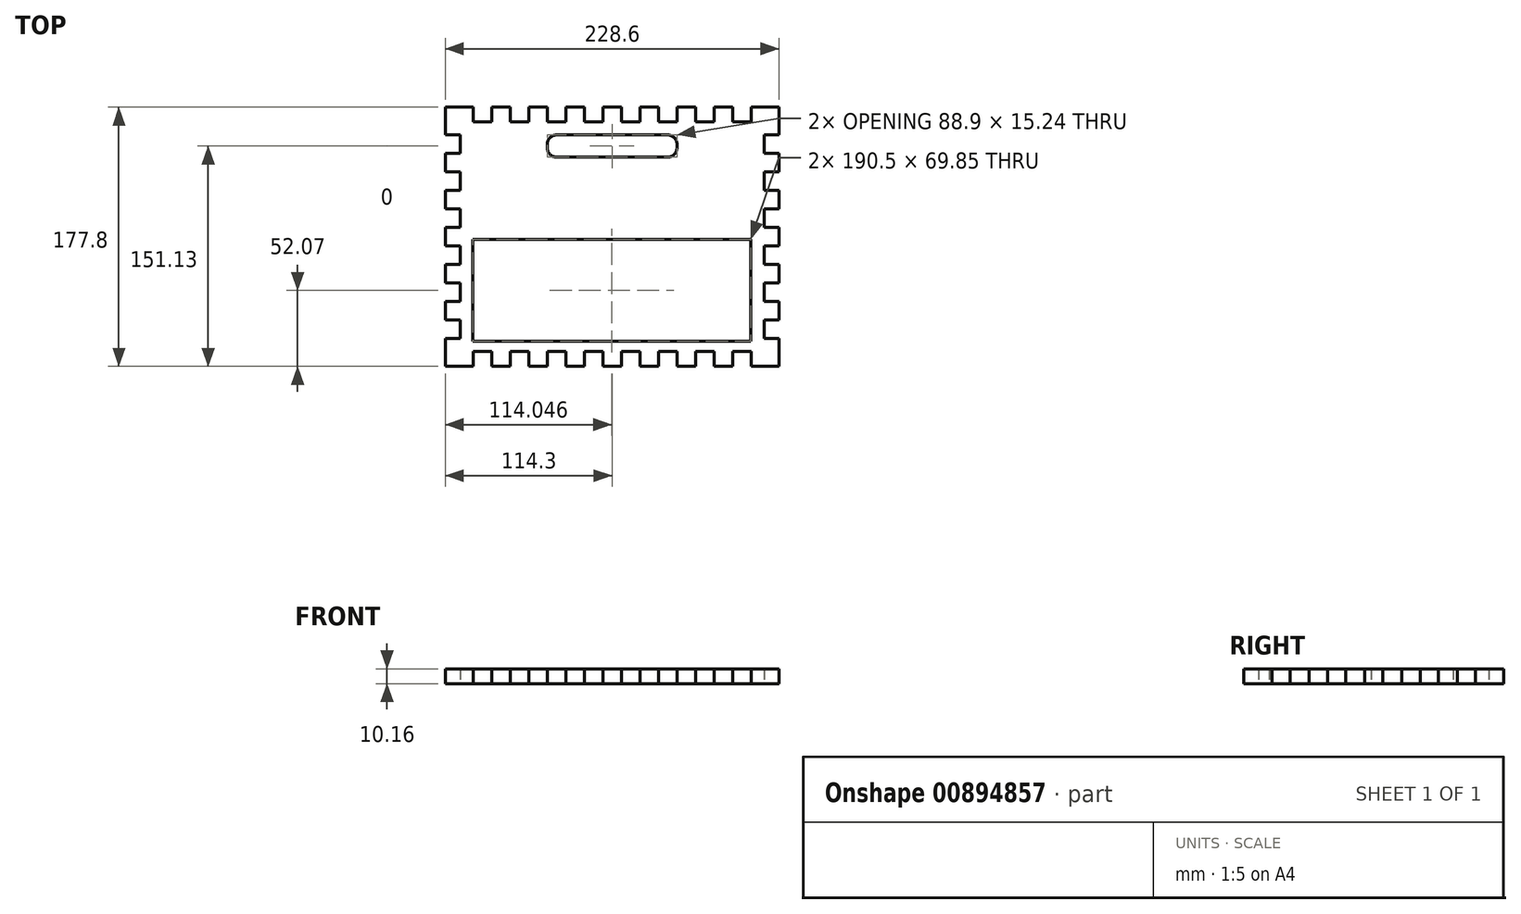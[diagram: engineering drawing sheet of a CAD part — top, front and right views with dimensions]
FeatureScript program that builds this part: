
annotation { "Feature Type Name" : "Feature", "Feature Type Description" : "" }
export const myFeature = defineFeature(function(context is Context, id is Id, definition is map)
    precondition{}
    {
        {
            var Q0;
            Q0=qCreatedBy(makeId("Top.planeOp"),FACE);
            var sketch = newSketch(context, id + "F0", { "sketchPlane" : qUnion([Q0])});
            skLineSegment(sketch, "E0.bottom", {"start": v(0, 0) * mm, "end": v(19.05, 0) * mm});
            skLineSegment(sketch, "E0.left", {"start": v(0, 0) * mm, "end": v(0, -19.05) * mm});
            skLineSegment(sketch, "E1", {"start": v(19.05, 0) * mm, "end": v(19.05, -10.16) * mm});
            skLineSegment(sketch, "E2", {"start": v(19.05, -10.16) * mm, "end": v(31.75, -10.16) * mm});
            skLineSegment(sketch, "E3", {"start": v(31.75, -10.16) * mm, "end": v(31.75, 0) * mm});
            skLineSegment(sketch, "E4", {"start": v(31.75, 0) * mm, "end": v(44.45, 0) * mm});
            skLineSegment(sketch, "E5", {"start": v(44.45, 0) * mm, "end": v(44.45, -10.16) * mm});
            skLineSegment(sketch, "E6", {"start": v(44.45, -10.16) * mm, "end": v(57.15, -10.16) * mm});
            skLineSegment(sketch, "E7", {"start": v(57.15, -10.16) * mm, "end": v(57.15, 0) * mm});
            skLineSegment(sketch, "E8", {"start": v(57.15, 0) * mm, "end": v(69.85, 0) * mm});
            skLineSegment(sketch, "E9", {"start": v(69.85, 0) * mm, "end": v(69.85, -10.16) * mm});
            skLineSegment(sketch, "E10", {"start": v(69.85, -10.16) * mm, "end": v(82.55, -10.16) * mm});
            skLineSegment(sketch, "E11", {"start": v(82.55, -10.16) * mm, "end": v(82.55, 0) * mm});
            skLineSegment(sketch, "E12", {"start": v(82.55, 0) * mm, "end": v(95.25, 0) * mm});
            skLineSegment(sketch, "E13", {"start": v(95.25, 0) * mm, "end": v(95.25, -10.16) * mm});
            skLineSegment(sketch, "E14", {"start": v(95.25, -10.16) * mm, "end": v(107.95, -10.16) * mm});
            skLineSegment(sketch, "E15", {"start": v(107.95, -10.16) * mm, "end": v(107.95, 0) * mm});
            skLineSegment(sketch, "E16.trimOffspring", {"start": v(107.95, 0) * mm, "end": v(120.65, 0) * mm});
            skLineSegment(sketch, "E17", {"start": v(120.65, 0) * mm, "end": v(120.65, -10.16) * mm});
            skLineSegment(sketch, "E18", {"start": v(120.65, -10.16) * mm, "end": v(133.35, -10.16) * mm});
            skLineSegment(sketch, "E19", {"start": v(133.35, -10.16) * mm, "end": v(133.35, 0) * mm});
            skLineSegment(sketch, "E20", {"start": v(133.35, 0) * mm, "end": v(146.05, 0) * mm});
            skLineSegment(sketch, "E21", {"start": v(146.05, 0) * mm, "end": v(146.05, -10.16) * mm});
            skLineSegment(sketch, "E22", {"start": v(146.05, -10.16) * mm, "end": v(158.75, -10.16) * mm});
            skLineSegment(sketch, "E23", {"start": v(158.75, -10.16) * mm, "end": v(158.75, 0) * mm});
            skLineSegment(sketch, "E24", {"start": v(158.75, 0) * mm, "end": v(171.45, 0) * mm});
            skLineSegment(sketch, "E25", {"start": v(171.45, 0) * mm, "end": v(171.45, -10.16) * mm});
            skLineSegment(sketch, "E26", {"start": v(171.45, -10.16) * mm, "end": v(184.15, -10.16) * mm});
            skLineSegment(sketch, "E27", {"start": v(184.15, -10.16) * mm, "end": v(184.15, 0) * mm});
            skLineSegment(sketch, "E28.trimOffspring", {"start": v(184.15, 0) * mm, "end": v(196.85, 0) * mm});
            skLineSegment(sketch, "E29", {"start": v(196.85, 0) * mm, "end": v(196.85, -10.16) * mm});
            skLineSegment(sketch, "E30", {"start": v(196.85, -10.16) * mm, "end": v(209.55, -10.16) * mm});
            skLineSegment(sketch, "E31", {"start": v(209.55, -10.16) * mm, "end": v(209.55, 0) * mm});
            skLineSegment(sketch, "E32.trimOffspring", {"start": v(209.55, 0) * mm, "end": v(228.6, 0) * mm});
            skLineSegment(sketch, "E33", {"start": v(0, -19.05) * mm, "end": v(10.16, -19.05) * mm});
            skLineSegment(sketch, "E34", {"start": v(10.16, -19.05) * mm, "end": v(10.16, -31.75) * mm});
            skLineSegment(sketch, "E35", {"start": v(10.16, -31.75) * mm, "end": v(0, -31.75) * mm});
            skLineSegment(sketch, "E36", {"start": v(0, -31.75) * mm, "end": v(0, -44.45) * mm});
            skLineSegment(sketch, "E37", {"start": v(0, -44.45) * mm, "end": v(10.16, -44.45) * mm});
            skLineSegment(sketch, "E38", {"start": v(10.16, -44.45) * mm, "end": v(10.16, -57.15) * mm});
            skLineSegment(sketch, "E39", {"start": v(10.16, -57.15) * mm, "end": v(0, -57.15) * mm});
            skLineSegment(sketch, "E40", {"start": v(0, -57.15) * mm, "end": v(0, -69.85) * mm});
            skLineSegment(sketch, "E41", {"start": v(0, -69.85) * mm, "end": v(10.16, -69.85) * mm});
            skLineSegment(sketch, "E42", {"start": v(10.16, -69.85) * mm, "end": v(10.16, -82.55) * mm});
            skLineSegment(sketch, "E43", {"start": v(10.16, -82.55) * mm, "end": v(0, -82.55) * mm});
            skLineSegment(sketch, "E44.trimOffspring", {"start": v(0, -82.55) * mm, "end": v(0, -95.25) * mm});
            skLineSegment(sketch, "E45", {"start": v(0, -95.25) * mm, "end": v(10.16, -95.25) * mm});
            skLineSegment(sketch, "E46", {"start": v(10.16, -95.25) * mm, "end": v(10.16, -107.95) * mm});
            skLineSegment(sketch, "E47", {"start": v(10.16, -107.95) * mm, "end": v(0, -107.95) * mm});
            skLineSegment(sketch, "E48", {"start": v(0, -107.95) * mm, "end": v(0, -120.65) * mm});
            skLineSegment(sketch, "E49", {"start": v(0, -120.65) * mm, "end": v(10.16, -120.65) * mm});
            skLineSegment(sketch, "E50", {"start": v(10.16, -120.65) * mm, "end": v(10.16, -133.35) * mm});
            skLineSegment(sketch, "E51", {"start": v(10.16, -133.35) * mm, "end": v(0, -133.35) * mm});
            skLineSegment(sketch, "E52", {"start": v(0, -133.35) * mm, "end": v(0, -146.05) * mm});
            skLineSegment(sketch, "E53", {"start": v(0, -146.05) * mm, "end": v(10.16, -146.05) * mm});
            skLineSegment(sketch, "E54", {"start": v(10.16, -146.05) * mm, "end": v(10.16, -158.75) * mm});
            skLineSegment(sketch, "E55", {"start": v(10.16, -158.75) * mm, "end": v(0, -158.75) * mm});
            skLineSegment(sketch, "E56.trimOffspring", {"start": v(0, -158.75) * mm, "end": v(0, -177.8) * mm});
            skLineSegment(sketch, "E57", {"start": v(114.3, 0) * mm, "end": v(114.3, 0) * mm});
            skLineSegment(sketch, "E58", {"start": v(0, -88.9) * mm, "end": v(0, -88.9) * mm});
            skLineSegment(sketch, "E59.MirrorCS", {"start": v(228.6, 0) * mm, "end": v(228.6, -19.05) * mm});
            skLineSegment(sketch, "E60.MirrorCS", {"start": v(228.6, -120.65) * mm, "end": v(218.44, -120.65) * mm});
            skLineSegment(sketch, "E61.MirrorCS", {"start": v(228.6, -82.55) * mm, "end": v(228.6, -95.25) * mm});
            skLineSegment(sketch, "E62.MirrorCS", {"start": v(218.44, -133.35) * mm, "end": v(228.6, -133.35) * mm});
            skLineSegment(sketch, "E63.MirrorCS", {"start": v(228.6, -44.45) * mm, "end": v(218.44, -44.45) * mm});
            skLineSegment(sketch, "E64.MirrorCS", {"start": v(218.44, -82.55) * mm, "end": v(228.6, -82.55) * mm});
            skLineSegment(sketch, "E65.MirrorCS", {"start": v(228.6, -146.05) * mm, "end": v(218.44, -146.05) * mm});
            skLineSegment(sketch, "E66.MirrorCS", {"start": v(218.44, -57.15) * mm, "end": v(228.6, -57.15) * mm});
            skLineSegment(sketch, "E67.MirrorCS", {"start": v(218.44, -158.75) * mm, "end": v(228.6, -158.75) * mm});
            skLineSegment(sketch, "E68.MirrorCS", {"start": v(228.6, -69.85) * mm, "end": v(218.44, -69.85) * mm});
            skLineSegment(sketch, "E69.MirrorCS", {"start": v(228.6, -95.25) * mm, "end": v(218.44, -95.25) * mm});
            skLineSegment(sketch, "E70.MirrorCS", {"start": v(218.44, -31.75) * mm, "end": v(228.6, -31.75) * mm});
            skLineSegment(sketch, "E71.MirrorCS", {"start": v(218.44, -107.95) * mm, "end": v(228.6, -107.95) * mm});
            skLineSegment(sketch, "E72.MirrorCS", {"start": v(228.6, -19.05) * mm, "end": v(218.44, -19.05) * mm});
            skLineSegment(sketch, "E73.MirrorCS", {"start": v(228.6, -57.15) * mm, "end": v(228.6, -69.85) * mm});
            skLineSegment(sketch, "E74.MirrorCS", {"start": v(228.6, -31.75) * mm, "end": v(228.6, -44.45) * mm});
            skLineSegment(sketch, "E75.MirrorCS", {"start": v(228.6, -107.95) * mm, "end": v(228.6, -120.65) * mm});
            skLineSegment(sketch, "E76.MirrorCS", {"start": v(228.6, -133.35) * mm, "end": v(228.6, -146.05) * mm});
            skLineSegment(sketch, "E77.MirrorCS", {"start": v(218.44, -69.85) * mm, "end": v(218.44, -82.55) * mm});
            skLineSegment(sketch, "E78.MirrorCS", {"start": v(218.44, -120.65) * mm, "end": v(218.44, -133.35) * mm});
            skLineSegment(sketch, "E79.MirrorCS", {"start": v(218.44, -95.25) * mm, "end": v(218.44, -107.95) * mm});
            skLineSegment(sketch, "E80.MirrorCS", {"start": v(218.44, -146.05) * mm, "end": v(218.44, -158.75) * mm});
            skLineSegment(sketch, "E81.MirrorCS", {"start": v(218.44, -44.45) * mm, "end": v(218.44, -57.15) * mm});
            skLineSegment(sketch, "E82.MirrorCS", {"start": v(218.44, -19.05) * mm, "end": v(218.44, -31.75) * mm});
            skLineSegment(sketch, "E83.MirrorCS", {"start": v(228.6, -158.75) * mm, "end": v(228.6, -177.8) * mm});
            skLineSegment(sketch, "E84.MirrorCS", {"start": v(0, -177.8) * mm, "end": v(19.05, -177.8) * mm});
            skLineSegment(sketch, "E85.MirrorCS", {"start": v(31.75, -177.8) * mm, "end": v(44.45, -177.8) * mm});
            skLineSegment(sketch, "E86.MirrorCS", {"start": v(184.15, -167.64) * mm, "end": v(184.15, -177.8) * mm});
            skLineSegment(sketch, "E87.MirrorCS", {"start": v(158.75, -167.64) * mm, "end": v(158.75, -177.8) * mm});
            skLineSegment(sketch, "E88.MirrorCS", {"start": v(196.85, -177.8) * mm, "end": v(196.85, -167.64) * mm});
            skLineSegment(sketch, "E89.MirrorCS", {"start": v(57.15, -167.64) * mm, "end": v(57.15, -177.8) * mm});
            skLineSegment(sketch, "E90.MirrorCS", {"start": v(120.65, -177.8) * mm, "end": v(120.65, -167.64) * mm});
            skLineSegment(sketch, "E91.MirrorCS", {"start": v(19.05, -177.8) * mm, "end": v(19.05, -167.64) * mm});
            skLineSegment(sketch, "E92.MirrorCS", {"start": v(95.25, -177.8) * mm, "end": v(95.25, -167.64) * mm});
            skLineSegment(sketch, "E93.MirrorCS", {"start": v(82.55, -167.64) * mm, "end": v(82.55, -177.8) * mm});
            skLineSegment(sketch, "E94.MirrorCS", {"start": v(44.45, -177.8) * mm, "end": v(44.45, -167.64) * mm});
            skLineSegment(sketch, "E95.MirrorCS", {"start": v(107.95, -177.8) * mm, "end": v(120.65, -177.8) * mm});
            skLineSegment(sketch, "E96.MirrorCS", {"start": v(209.55, -167.64) * mm, "end": v(209.55, -177.8) * mm});
            skLineSegment(sketch, "E97.MirrorCS", {"start": v(146.05, -177.8) * mm, "end": v(146.05, -167.64) * mm});
            skLineSegment(sketch, "E98.MirrorCS", {"start": v(31.75, -167.64) * mm, "end": v(31.75, -177.8) * mm});
            skLineSegment(sketch, "E99.MirrorCS", {"start": v(171.45, -177.8) * mm, "end": v(171.45, -167.64) * mm});
            skLineSegment(sketch, "E100.MirrorCS", {"start": v(133.35, -167.64) * mm, "end": v(133.35, -177.8) * mm});
            skLineSegment(sketch, "E101.MirrorCS", {"start": v(107.95, -167.64) * mm, "end": v(107.95, -177.8) * mm});
            skLineSegment(sketch, "E102.MirrorCS", {"start": v(69.85, -177.8) * mm, "end": v(69.85, -167.64) * mm});
            skLineSegment(sketch, "E103.MirrorCS", {"start": v(57.15, -177.8) * mm, "end": v(69.85, -177.8) * mm});
            skLineSegment(sketch, "E104.MirrorCS", {"start": v(133.35, -177.8) * mm, "end": v(146.05, -177.8) * mm});
            skLineSegment(sketch, "E105.MirrorCS", {"start": v(158.75, -177.8) * mm, "end": v(171.45, -177.8) * mm});
            skLineSegment(sketch, "E106.MirrorCS", {"start": v(82.55, -177.8) * mm, "end": v(95.25, -177.8) * mm});
            skLineSegment(sketch, "E107.MirrorCS", {"start": v(184.15, -177.8) * mm, "end": v(196.85, -177.8) * mm});
            skLineSegment(sketch, "E108.MirrorCS", {"start": v(171.45, -167.64) * mm, "end": v(184.15, -167.64) * mm});
            skLineSegment(sketch, "E109.MirrorCS", {"start": v(146.05, -167.64) * mm, "end": v(158.75, -167.64) * mm});
            skLineSegment(sketch, "E110.MirrorCS", {"start": v(196.85, -167.64) * mm, "end": v(209.55, -167.64) * mm});
            skLineSegment(sketch, "E111.MirrorCS", {"start": v(44.45, -167.64) * mm, "end": v(57.15, -167.64) * mm});
            skLineSegment(sketch, "E112.MirrorCS", {"start": v(69.85, -167.64) * mm, "end": v(82.55, -167.64) * mm});
            skLineSegment(sketch, "E113.MirrorCS", {"start": v(120.65, -167.64) * mm, "end": v(133.35, -167.64) * mm});
            skLineSegment(sketch, "E114.MirrorCS", {"start": v(19.05, -167.64) * mm, "end": v(31.75, -167.64) * mm});
            skLineSegment(sketch, "E115.MirrorCS", {"start": v(95.25, -167.64) * mm, "end": v(107.95, -167.64) * mm});
            skLineSegment(sketch, "E116.MirrorCS", {"start": v(209.55, -177.8) * mm, "end": v(228.6, -177.8) * mm});
            skLineSegment(sketch, "E117.bottom", {"start": v(18.8, -90.8) * mm, "end": v(209.3, -90.8) * mm});
            skLineSegment(sketch, "E117.top", {"start": v(18.8, -160.66) * mm, "end": v(209.3, -160.66) * mm});
            skLineSegment(sketch, "E117.left", {"start": v(18.8, -90.8) * mm, "end": v(18.8, -160.66) * mm});
            skLineSegment(sketch, "E117.right", {"start": v(209.3, -90.8) * mm, "end": v(209.3, -160.66) * mm});
            skLineSegment(sketch, "E118.bottom", {"start": v(76.2, -19.05) * mm, "end": v(152.4, -19.05) * mm});
            skLineSegment(sketch, "E118.top", {"start": v(76.2, -34.3) * mm, "end": v(152.4, -34.3) * mm});
            skLineSegment(sketch, "E118.left", {"start": v(69.85, -25.4) * mm, "end": v(69.85, -27.94) * mm});
            skLineSegment(sketch, "E118.right", {"start": v(158.75, -25.4) * mm, "end": v(158.75, -27.94) * mm});
            skLineSegment(sketch, "E119", {"start": v(114.3, -19.05) * mm, "end": v(114.3, 0) * mm, "construction": true});
            skPoint(sketch, "E120.visualSharp", {"position": v(158.75, -19.05) * mm});
            skArc(sketch, "E120.filletArc", {"start": v(158.75, -25.4) * mm, "mid": v(156.9, -20.9) * mm, "end": v(152.4, -19.05) * mm});
            skPoint(sketch, "E121.visualSharp", {"position": v(158.75, -34.3) * mm});
            skArc(sketch, "E121.filletArc", {"start": v(152.4, -34.3) * mm, "mid": v(156.9, -32.43) * mm, "end": v(158.75, -27.94) * mm});
            skPoint(sketch, "E122.visualSharp", {"position": v(69.85, -19.05) * mm});
            skArc(sketch, "E122.filletArc", {"start": v(76.2, -19.05) * mm, "mid": v(71.7, -20.9) * mm, "end": v(69.85, -25.4) * mm});
            skPoint(sketch, "E123.visualSharp", {"position": v(69.85, -34.3) * mm});
            skArc(sketch, "E123.filletArc", {"start": v(69.85, -27.94) * mm, "mid": v(71.7, -32.43) * mm, "end": v(76.2, -34.3) * mm});
            skSolve(sketch);
        }
        {
            var Q0;
            Q0=makeQuery(id+"F0.imprint","IMPRINT",FACE,{"disambiguationData":[TD([[makeQuery(id+"F0.imprint","IMPRINT",EDGE,{"derivedFrom":sQuery(id+"F0.wireOp",EDGE,"E0.bottom")}),-1.0]])]});
            extrude(context, id + "F1", {"entities" : qUnion([Q0]), "depth" : 10.16 * mm, "offsetDistance" : 25.4 * mm});
        }
        {
            var Q0;
            Q0 = qSketchRegion(id + "F0", true);
            extrude(context, id + "F2", {"entities" : qUnion([Q0]), "depth" : 10.16 * mm, "offsetDistance" : 25.4 * mm});
        }
    });
